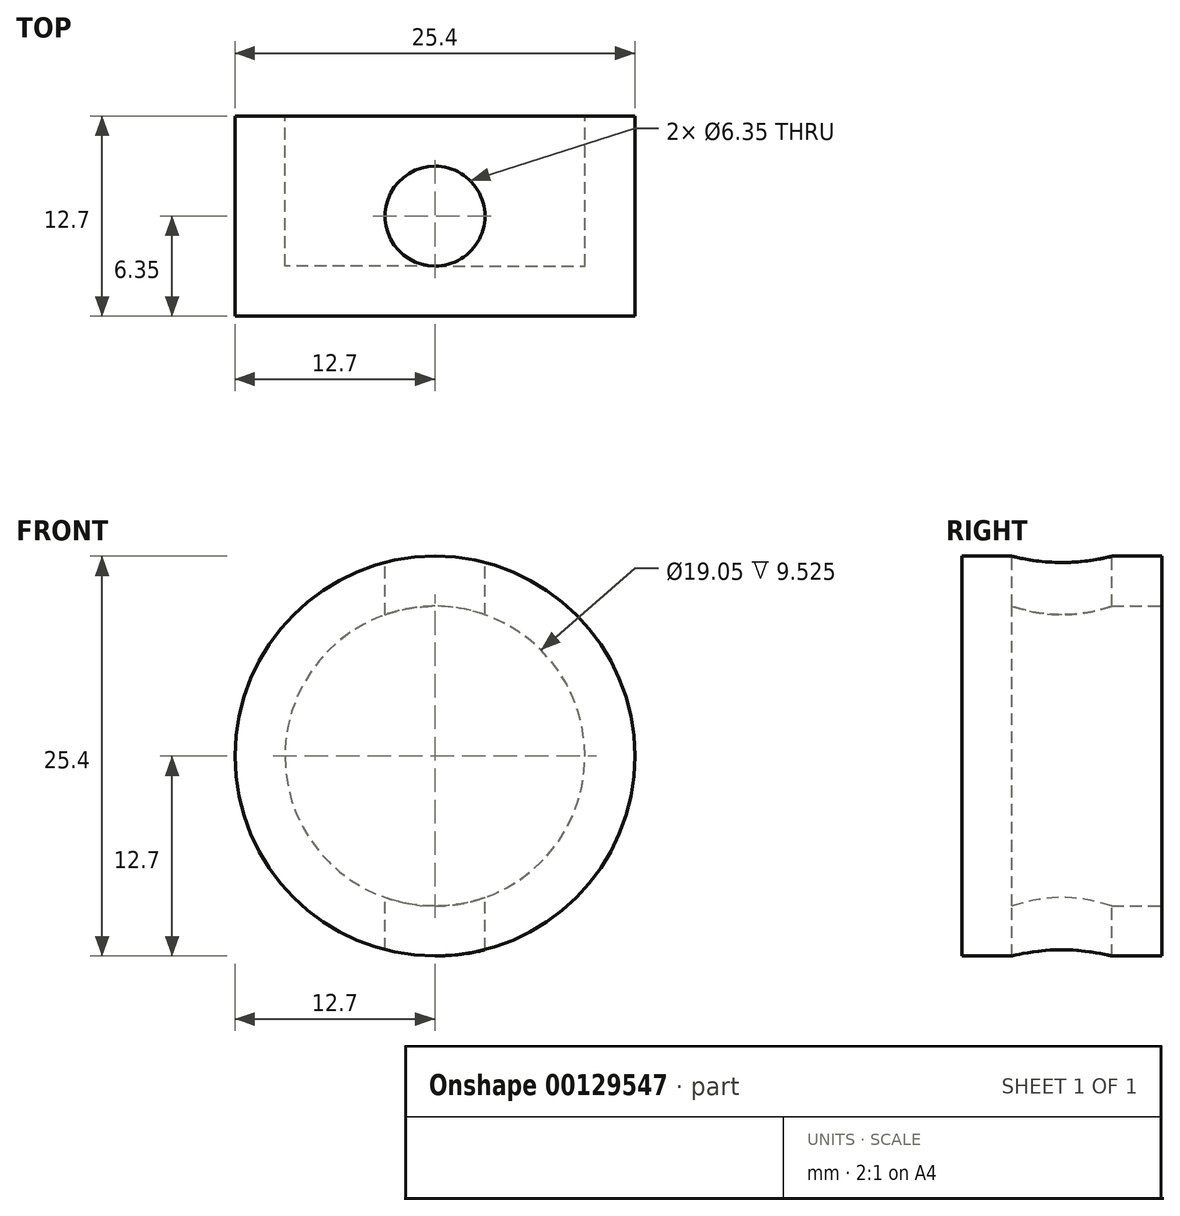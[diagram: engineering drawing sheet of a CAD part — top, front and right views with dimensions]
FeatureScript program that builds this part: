
annotation { "Feature Type Name" : "Feature", "Feature Type Description" : "" }
export const myFeature = defineFeature(function(context is Context, id is Id, definition is map)
    precondition{}
    {
        {
            var Q0;
            Q0=qCreatedBy(makeId("Front.planeOp"),FACE);
            var sketch = newSketch(context, id + "F0", { "sketchPlane" : qUnion([Q0])});
            skLineSegment(sketch, "E0.bottom", {"start": v(12.7, -12.7) * mm, "end": v(-12.7, -12.7) * mm});
            skLineSegment(sketch, "E0.top", {"start": v(12.7, 12.7) * mm, "end": v(-12.7, 12.7) * mm});
            skLineSegment(sketch, "E0.left", {"start": v(12.7, -12.7) * mm, "end": v(12.7, 12.7) * mm});
            skLineSegment(sketch, "E0.right", {"start": v(-12.7, -12.7) * mm, "end": v(-12.7, 12.7) * mm});
            skPoint(sketch, "E0.middle", {"position": v(0, 0) * mm});
            skSolve(sketch);
        }
        {
            var Q0;
            Q0 = qSketchRegion(id + "F0", true);
            extrude(context, id + "F1", {"entities" : qUnion([Q0]), "depth" : 12.7 * mm});
        }
        {
            var Q0;
            Q0=makeQuery(id+"F1.opExtrude","SWEPT_FACE",FACE,{"disambiguationData":[OSD([sQuery(id+"F0.wireOp",EDGE,"E0.top")])]});
            var sketch = newSketch(context, id + "F2", { "sketchPlane" : qUnion([Q0])});
            skCircle(sketch, "E1", {"center": v(0, -6.35) * mm, "radius": 3.18 * mm});
            skPoint(sketch, "E1.centerSnap0", {"position": v(-12.7, -6.35) * mm});
            skPoint(sketch, "E1.centerSnap1", {"position": v(0, -12.7) * mm});
            skSolve(sketch);
        }
        {
            var Q0;
            Q0=makeQuery(id+"F2.imprint","IMPRINT",FACE,{"disambiguationData":[TD([[makeQuery(id+"F2.imprint","IMPRINT",EDGE,{"derivedFrom":sQuery(id+"F2.wireOp",EDGE,"E1")}),1.0]])]});
            extrude(context, id + "F3", {"entities" : qUnion([Q0]), "operationType" : NewBodyOperationType.REMOVE, "oppositeDirection" : true, "depth" : 25.4 * mm});
        }
        {
            var Q0;
            Q0=makeQuery(id+"F1.opExtrude","CAP_FACE",FACE,{"disambiguationData":[OSD([sQuery(id+"F0.wireOp",EDGE,"E0.bottom"),sQuery(id+"F0.wireOp",EDGE,"E0.top"),sQuery(id+"F0.wireOp",EDGE,"E0.left"),sQuery(id+"F0.wireOp",EDGE,"E0.right")])],"isStart":true});
            var sketch = newSketch(context, id + "F4", { "sketchPlane" : qUnion([Q0])});
            skCircle(sketch, "E2", {"center": v(0, 0) * mm, "radius": 12.7 * mm});
            skSolve(sketch);
        }
        {
            var Q0;
            Q0 = qSketchRegion(id + "F4", true);
            extrude(context, id + "F5", {"entities" : qUnion([Q0]), "operationType" : NewBodyOperationType.INTERSECT, "oppositeDirection" : true, "depth" : 25.4 * mm});
        }
        {
            var Q0;
            Q0=makeQuery(id+"F1.opExtrude","CAP_FACE",FACE,{"disambiguationData":[OSD([sQuery(id+"F0.wireOp",EDGE,"E0.bottom"),sQuery(id+"F0.wireOp",EDGE,"E0.top"),sQuery(id+"F0.wireOp",EDGE,"E0.left"),sQuery(id+"F0.wireOp",EDGE,"E0.right")])],"isStart":true});
            var sketch = newSketch(context, id + "F6", { "sketchPlane" : qUnion([Q0])});
            skCircle(sketch, "E3", {"center": v(0, 0) * mm, "radius": 9.53 * mm});
            skSolve(sketch);
        }
        {
            var Q0;
            Q0 = qSketchRegion(id + "F6", true);
            extrude(context, id + "F7", {"entities" : qUnion([Q0]), "operationType" : NewBodyOperationType.REMOVE, "oppositeDirection" : true, "depth" : 9.52 * mm});
        }
    });
